# Revit family: A61_63_UN_Line Pendant_ETK
name_source: partatom
category: Lighting Fixtures
units: mm (PartAtom-declared; Revit-internal decimal feet)

## family parameters
Always vertical = Yes
Cut with Voids When Loaded = No
Light Source = Yes
OmniClass Number = 23.80.70.11.14.11
OmniClass Title = Downlights
Part Type = Normal
Room Calculation Point = Yes
Round Connector Dimension = Use Diameter
Shared = No
Work Plane-Based = No

## types (56) — shared parameters
Assembly Code = 63.0
Color Filter = 16777215
Dimming Lamp Color Temperature Shift = <None>
ETIM Code = ETIMCODE
Emit Shape Visible in Rendering = No
Emit from Rectangle Length = 41 mm  [stored 0.134514 ft]
GTIN Code = GTINCODE
H1 = 82 mm  [stored 0.269029 ft]
Housing_Material = Select RGB Value for different appearance
IK Value = -
IP Value = IP20
ISBN Code = ISBNCODE
IfcExportAs = IfcLightFixtureType
IfcExportType = USERDEFINED
L2 = 45 mm  [stored 0.147638 ft]
L3 = 2 mm  [stored 0.00656168 ft]
LED Panel = Yes
Lamp = LED
Model = A61
Tilt Angle = 90.00°
Type Comments = Line Pendant
URL = www.etk.nl
Voltage = 230 V
zero-valued in all types: Calc_L2_Symbol

## per-type parameters (varying)
| type | Apparent Load | Calc_L1_Symbol | Emit from Rectangle Width | L1 | L4 | Luminous Flux (lm) | Manufacturer | Photometric Web File | Wattage Comments |
| A61.2 LED 82W 4000K 12000Lm zwart mat RAL9005 DALI voedingsmodule 2805mm LINEpro light pendel (A6-604PL.A280.40.06/DIMM 2-3) | 82 VA | 28 mm | 2801 mm  [stored 9.18963 ft] | 2805 mm  [stored 9.20276 ft] | 2605 mm  [stored 8.54659 ft] | 6618 lm | ETK B.V. | A61.2863.35_LDT.ies | 82 |
| A61.2 LED 82W 4000K 12000Lm wit mat RAL9003 DALI voedingsmodule 2805mm LINEpro light pendel (A6-604PL.A280.40.08/DIMM 2-3) | 82 VA | 28 mm | 2801 mm  [stored 9.18963 ft] | 2805 mm  [stored 9.20276 ft] | 2605 mm  [stored 8.54659 ft] | 6618 lm | ETK B.V. | A61.2863.15_LDT.ies | 82 |
| A61.2 LED 82W 4000K 12000Lm wit mat RAL9003 voedingsmodule 2805mm LINEpro light pendel (A6-604PL.A280.40.08) | 82 VA | 28 mm | 2801 mm  [stored 9.18963 ft] | 2805 mm  [stored 9.20276 ft] | 2605 mm  [stored 8.54659 ft] | 6618 lm | ETK B.V. | A61.2860.15_LDT.ies | 82 |
| A61.2 LED 82W 4000K 12000Lm zwart mat RAL9005 voedingsmodule 2805mm LINEpro light pendel (A6-604PL.A280.40.06) | 82 VA | 28 mm | 2801 mm  [stored 9.18963 ft] | 2805 mm  [stored 9.20276 ft] | 2605 mm  [stored 8.54659 ft] | 6618 lm | ETK B.V. | A61.2860.35_LDT.ies | 82 |
| A61.2 LED 82W 3000K 11510Lm zwart mat RAL9005 voedingsmodule 2805mm LINEpro light pendel (A6-604PL.A280.30.06) | 82 VA | 28 mm | 2801 mm  [stored 9.18963 ft] | 2805 mm  [stored 9.20276 ft] | 2605 mm  [stored 8.54659 ft] | 6346 lm | ETK B.V. | A61.2810.35_LDT.ies | 82 |
| A61.2 LED 82W 3000K 11510Lm wit mat RAL9003 voedingsmodule 2805mm LINEpro light pendel (A6-604PL.A280.30.08) | 82 VA | 28 mm | 2801 mm  [stored 9.18963 ft] | 2805 mm  [stored 9.20276 ft] | 2605 mm  [stored 8.54659 ft] | 6346 lm | ETK B.V. | A61.2810.15_LDT.ies | 82 |
| A61.2 LED 82W 3000K 11510Lm wit mat RAL9003 DALI voedingsmodule 2805mm LINEpro light pendel (A6-604PL.A280.30.08/DIMM 2-3) | 82 VA | 28 mm | 2801 mm  [stored 9.18963 ft] | 2805 mm  [stored 9.20276 ft] | 2605 mm  [stored 8.54659 ft] | 6346 lm | ETK B.V. | A61.2813.15_LDT.ies | 82 |
| A61.2 LED 82W 3000K 11510Lm zwart mat RAL9005 DALI voedingsmodule 2805mm LINEpro light pendel (A6-604PL.A280.30.06/DIMM 2-3) | 82 VA | 28 mm | 2801 mm  [stored 9.18963 ft] | 2805 mm  [stored 9.20276 ft] | 2605 mm  [stored 8.54659 ft] | 6346 lm | ETK B.V. | A61.2813.35_LDT.ies | 82 |
| A61.2 LED 75W 4000K 10800Lm wit mat RAL9003 voedingsmodule 2525mm LINEpro light pendel (A6-604PL.A252.40.08) | 75 VA | 25 mm  [stored 0.082021 ft] | 2521 mm | 2525 mm  [stored 8.28412 ft] | 2325 mm | 5956 lm | ETK B.V. | A61.2760.15_LDT.ies | 75 |
| A61.2 LED 75W 4000K 10800Lm wit mat RAL9003 DALI voedingsmodule 2525mm LINEpro light pendel (A6-604PL.A252.40.08/DIMM 2-3) | 75 VA | 25 mm  [stored 0.082021 ft] | 2521 mm | 2525 mm  [stored 8.28412 ft] | 2325 mm | 5956 lm | ETK B.V. | A61.2763.15_LDT.ies | 75 |
| A61.2 LED 75W 4000K 10800Lm zwart mat RAL9005 voedingsmodule 2525mm LINEpro light pendel (A6-604PL.A252.40.06) | 75 VA | 25 mm  [stored 0.082021 ft] | 2521 mm | 2525 mm  [stored 8.28412 ft] | 2325 mm | 5956 lm | ETK B.V. | A61.2760.35_LDT.ies | 75 |
| A61.2 LED 75W 4000K 10800Lm zwart mat RAL9005 DALI voedingsmodule 2525mm LINEpro light pendel (A6-604PL.A252.40.06/DIMM 2-3) | 75 VA | 25 mm  [stored 0.082021 ft] | 2521 mm | 2525 mm  [stored 8.28412 ft] | 2325 mm | 5956 lm | ETK B.V. | A61.2763.35_LDT.ies | 75 |
| A61.2 LED 75W 3000K 10360Lm zwart mat RAL9005 voedingsmodule 2525mm LINEpro light pendel (A6-604PL.A252.30.06) | 75 VA | 25 mm  [stored 0.082021 ft] | 2521 mm | 2525 mm  [stored 8.28412 ft] | 2325 mm | 5712 lm | ETK B.V. | A61.2710.35_LDT.ies | 75 |
| A61.2 LED 75W 3000K 10360Lm wit mat RAL9003 DALI voedingsmodule 2525mm LINEpro light pendel (A6-604PL.A252.30.08/DIMM 2-3) | 75 VA | 25 mm  [stored 0.082021 ft] | 2521 mm | 2525 mm  [stored 8.28412 ft] | 2325 mm | 5712 lm | ETK B.V. | A61.2713.15_LDT.ies | 75 |
| A61.2 LED 75W 3000K 10360Lm zwart mat RAL9005 DALI voedingsmodule 2525mm LINEpro light pendel (A6-604PL.A252.30.06/DIMM 2-3) | 75 VA | 25 mm  [stored 0.082021 ft] | 2521 mm | 2525 mm  [stored 8.28412 ft] | 2325 mm | 5712 lm | ETK B.V. | A61.2713.35_LDT.ies | 75 |
| A61.2 LED 75W 3000K 10360Lm wit mat RAL9003 voedingsmodule 2525mm LINEpro light pendel (A6-604PL.A252.30.08) | 75 VA | 25 mm  [stored 0.082021 ft] | 2521 mm | 2525 mm  [stored 8.28412 ft] | 2325 mm | 5712 lm | ETK B.V. | A61.2710.15_LDT.ies | 75 |
| A61.2 LED 67W 4000K 9600Lm zwart mat RAL9005 voedingsmodule 2245mm LINEpro light pendel (A6-604PL.A224.40.06) | 67 VA | 22 mm | 2241 mm  [stored 7.35236 ft] | 2245 mm  [stored 7.36549 ft] | 2045 mm  [stored 6.70932 ft] | 5294 lm | ETK B.V. | A61.2660.35_LDT.ies | 67 |
| A61.2 LED 67W 4000K 9600Lm wit mat RAL9003 DALI voedingsmodule 2245mm LINEpro light pendel (A6-604PL.A224.40.08/DIMM 2-3) | 67 VA | 22 mm | 2241 mm  [stored 7.35236 ft] | 2245 mm  [stored 7.36549 ft] | 2045 mm  [stored 6.70932 ft] | 5294 lm | ETK B.V. | A61.2663.15_LDT.ies | 67 |
| A61.2 LED 67W 4000K 9600Lm wit mat RAL9003 voedingsmodule 2245mm LINEpro light pendel (A6-604PL.A224.40.08) | 67 VA | 22 mm | 2241 mm  [stored 7.35236 ft] | 2245 mm  [stored 7.36549 ft] | 2045 mm  [stored 6.70932 ft] | 5294 lm | ETK B.V. | A61.2660.15_LDT.ies | 67 |
| A61.2 LED 67W 4000K 9600Lm zwart mat RAL9005 DALI voedingsmodule 2245mm LINEpro light pendel (A6-604PL.A224.40.06/DIMM 2-3) | 67 VA | 22 mm | 2241 mm  [stored 7.35236 ft] | 2245 mm  [stored 7.36549 ft] | 2045 mm  [stored 6.70932 ft] | 5294 lm | ETK B.V. | A61.2663.35_LDT.ies | 67 |
| A61.2 LED 67W 3000K 9205Lm zwart mat RAL9005 voedingsmodule 2245mm LINEpro light pendel (A6-604PL.A224.30.06) | 67 VA | 22 mm | 2241 mm  [stored 7.35236 ft] | 2245 mm  [stored 7.36549 ft] | 2045 mm  [stored 6.70932 ft] | 5078 lm | ETK B.V. | A61.2610.35_LDT.ies | 67 |
| A61.2 LED 67W 3000K 9205Lm wit mat RAL9003 DALI voedingsmodule 2245mm LINEpro light pendel (A6-604PL.A224.30.08/DIMM 2-3) | 67 VA | 22 mm | 2241 mm  [stored 7.35236 ft] | 2245 mm  [stored 7.36549 ft] | 2045 mm  [stored 6.70932 ft] | 5078 lm | ETK B.V. | A61.2613.15_LDT.ies | 67 |
| A61.2 LED 67W 3000K 9205Lm wit mat RAL9003 voedingsmodule 2245mm LINEpro light pendel (A6-604PL.A224.30.08) | 67 VA | 22 mm | 2241 mm  [stored 7.35236 ft] | 2245 mm  [stored 7.36549 ft] | 2045 mm  [stored 6.70932 ft] | 5078 lm | ETK B.V. | A61.2610.15_LDT.ies | 67 |
| A61.2 LED 67W 3000K 9205Lm zwart mat RAL9005 DALI voedingsmodule 2245mm LINEpro light pendel (A6-604PL.A224.30.06/DIMM 2-3) | 67 VA | 22 mm | 2241 mm  [stored 7.35236 ft] | 2245 mm  [stored 7.36549 ft] | 2045 mm  [stored 6.70932 ft] | 5078 lm | ETK B.V. | A61.2613.35_LDT.ies | 67 |
| A61.2 LED 60W 4000K 8400Lm wit mat RAL9003 DALI voedingsmodule 1965mm LINEpro light pendel (A6-604PL.A196.40.08/DIMM 2-3) | 60 VA | 20 mm  [stored 0.0656168 ft] | 1961 mm  [stored 6.43373 ft] | 1965 mm  [stored 6.44685 ft] | 1765 mm  [stored 5.79068 ft] | 4633 lm | ETK B.V. | A61.2563.15_LDT.ies | 60 |
| A61.2 LED 60W 4000K 8400Lm zwart mat RAL9005 voedingsmodule 1965mm LINEpro light pendel (A6-604PL.A196.40.06) | 60 VA | 20 mm  [stored 0.0656168 ft] | 1961 mm  [stored 6.43373 ft] | 1965 mm  [stored 6.44685 ft] | 1765 mm  [stored 5.79068 ft] | 4633 lm | ETK B.V. | A61.2560.35_LDT.ies | 60 |
| A61.2 LED 60W 4000K 8400Lm wit mat RAL9003 voedingsmodule 1965mm LINEpro light pendel (A6-604PL.A196.40.08) | 60 VA | 20 mm  [stored 0.0656168 ft] | 1961 mm  [stored 6.43373 ft] | 1965 mm  [stored 6.44685 ft] | 1765 mm  [stored 5.79068 ft] | 4633 lm | ETK B.V. | A61.2560.15_LDT.ies | 60 |
| A61.2 LED 60W 4000K 8400Lm zwart mat RAL9005 DALI voedingsmodule 1965mm LINEpro light pendel (A6-604PL.A196.40.06/DIMM 2-3) | 60 VA | 20 mm  [stored 0.0656168 ft] | 1961 mm  [stored 6.43373 ft] | 1965 mm  [stored 6.44685 ft] | 1765 mm  [stored 5.79068 ft] | 4633 lm | ETK B.V. | A61.2563.35_LDT.ies | 60 |
| A61.2 LED 60W 3000K 8055Lm wit mat RAL9003 voedingsmodule 1965mm LINEpro light pendel (A6-604PL.A196.30.08) | 60 VA | 20 mm  [stored 0.0656168 ft] | 1961 mm  [stored 6.43373 ft] | 1965 mm  [stored 6.44685 ft] | 1765 mm  [stored 5.79068 ft] | 4442 lm | ETK B.V. | A61.2510.15_LDT.ies | 60 |
| A61.2 LED 60W 3000K 8055Lm zwart mat RAL9005 voedingsmodule 1965mm LINEpro light pendel (A6-604PL.A196.30.06) | 60 VA | 20 mm  [stored 0.0656168 ft] | 1961 mm  [stored 6.43373 ft] | 1965 mm  [stored 6.44685 ft] | 1765 mm  [stored 5.79068 ft] | 4442 lm | ETK B.V. | A61.2510.35_LDT.ies | 60 |
| A61.2 LED 60W 3000K 8055Lm zwart mat RAL9005 DALI voedingsmodule 1965mm LINEpro light pendel (A6-604PL.A196.30.06/DIMM 2-3) | 60 VA | 20 mm  [stored 0.0656168 ft] | 1961 mm  [stored 6.43373 ft] | 1965 mm  [stored 6.44685 ft] | 1765 mm  [stored 5.79068 ft] | 4442 lm | ETK B.V. | A61.2513.35_LDT.ies | 60 |
| A61.2 LED 60W 3000K 8055Lm wit mat RAL9003 DALI voedingsmodule 1965mm LINEpro light pendel (A6-604PL.A196.30.08/DIMM 2-3) | 60 VA | 20 mm  [stored 0.0656168 ft] | 1961 mm  [stored 6.43373 ft] | 1965 mm  [stored 6.44685 ft] | 1765 mm  [stored 5.79068 ft] | 4442 lm | ETK B.V. | A61.2513.15_LDT.ies | 60 |
| A61.2 LED 51W 4000K 7200Lm wit mat RAL9003 voedingsmodule 1685mm LINEpro light pendel (A6-604PL.A168.40.08) | 51 VA | 17 mm | 1681 mm  [stored 5.51509 ft] | 1685 mm  [stored 5.52822 ft] | 1485 mm  [stored 4.87205 ft] | 3971 lm | ETK B.V. | A61.2460.15_LDT.ies | 51 |
| A61.2 LED 51W 4000K 7200Lm wit mat RAL9003 DALI voedingsmodule 1685mm LINEpro light pendel (A6-604PL.A168.40.08/DIMM 2-3) | 51 VA | 17 mm | 1681 mm  [stored 5.51509 ft] | 1685 mm  [stored 5.52822 ft] | 1485 mm  [stored 4.87205 ft] | 3971 lm | ETK B.V. | A61.2463.15_LDT.ies | 51 |
| A61.2 LED 51W 4000K 7200Lm zwart mat RAL9005 DALI voedingsmodule 1685mm LINEpro light pendel (A6-604PL.A168.40.06/DIMM 2-3) | 51 VA | 17 mm | 1681 mm  [stored 5.51509 ft] | 1685 mm  [stored 5.52822 ft] | 1485 mm  [stored 4.87205 ft] | 3971 lm | ETK B.V. | A61.2463.35_LDT.ies | 51 |
| A61.2 LED 51W 4000K 7200Lm zwart mat RAL9005 voedingsmodule 1685mm LINEpro light pendel (A6-604PL.A168.40.06) | 51 VA | 17 mm | 1681 mm  [stored 5.51509 ft] | 1685 mm  [stored 5.52822 ft] | 1485 mm  [stored 4.87205 ft] | 3971 lm | ETK B.V. | A61.2460.35_LDT.ies | 51 |
| A61.2 LED 51W 3000K 6905Lm wit mat RAL9003 DALI voedingsmodule 1685mm LINEpro light pendel (A6-604PL.A168.30.08/DIMM 2-3) | 51 VA | 17 mm | 1681 mm  [stored 5.51509 ft] | 1685 mm  [stored 5.52822 ft] | 1485 mm  [stored 4.87205 ft] | 3808 lm | ETK B.V. | A61.2413.15_LDT.ies | 51 |
| A61.2 LED 51W 3000K 6905Lm zwart mat RAL9005 voedingsmodule 1685mm LINEpro light pendel (A6-604PL.A168.30.06) | 51 VA | 17 mm | 1681 mm  [stored 5.51509 ft] | 1685 mm  [stored 5.52822 ft] | 1485 mm  [stored 4.87205 ft] | 3808 lm | ETK B.V. | A61.2410.35_LDT.ies | 51 |
| A61.2 LED 51W 3000K 6905Lm wit mat RAL9003 voedingsmodule 1685mm LINEpro light pendel (A6-604PL.A168.30.08) | 51 VA | 17 mm | 1681 mm  [stored 5.51509 ft] | 1685 mm  [stored 5.52822 ft] | 1485 mm  [stored 4.87205 ft] | 3808 lm | ETK B.V. | A61.2410.15_LDT.ies | 51 |
| A61.2 LED 51W 3000K 6905Lm zwart mat RAL9005 DALI voedingsmodule 1685mm LINEpro light pendel (A6-604PL.A168.30.06/DIMM 2-3) | 51 VA | 17 mm | 1681 mm  [stored 5.51509 ft] | 1685 mm  [stored 5.52822 ft] | 1485 mm  [stored 4.87205 ft] | 3808 lm | ETK B.V. | A61.2413.35_LDT.ies | 51 |
| A61.2 LED 44W 3000K 5755Lm zwart mat RAL9005 voedingsmodule 1405mm LINEpro light pendel (A6-604PL.A140.30.06) | 44 VA | 14 mm  [stored 0.0459318 ft] | 1401 mm | 1405 mm  [stored 4.60958 ft] | 1205 mm  [stored 3.95341 ft] | 3173 lm | ETK B.V. | A61.2310.35_LDT.ies | 44 |
| A61.2 LED 44W 3000K 5755Lm wit mat RAL9003 DALI voedingsmodule 1405mm LINEpro light pendel (A6-604PL.A140.30.08/DIMM 2-3) | 44 VA | 14 mm  [stored 0.0459318 ft] | 1401 mm | 1405 mm  [stored 4.60958 ft] | 1205 mm  [stored 3.95341 ft] | 3173 lm | ETK B.V. | A61.2313.15_LDT.ies | 44 |
| A61.2 LED 44W 3000K 5755Lm zwart mat RAL9005 DALI voedingsmodule 1405mm LINEpro light pendel (A6-604PL.A140.30.06/DIMM 2-3) | 44 VA | 14 mm  [stored 0.0459318 ft] | 1401 mm | 1405 mm  [stored 4.60958 ft] | 1205 mm  [stored 3.95341 ft] | 3173 lm | ETK B.V. | A61.2313.35_LDT.ies | 44 |
| A61.2 LED 44W 3000K 5755Lm wit mat RAL9003 voedingsmodule 1405mm LINEpro light pendel (A6-604PL.A140.30.08) | 44 VA | 14 mm  [stored 0.0459318 ft] | 1401 mm | 1405 mm  [stored 4.60958 ft] | 1205 mm  [stored 3.95341 ft] | 3173 lm | ETK B.V. | A61.2310.15_LDT.ies | 44 |
| A61.2 LED 44W 4000K 6000Lm zwart mat RAL9005 voedingsmodule 1405mm LINEpro light pendel (A6-604PL.A140.40.06) | 44 VA | 14 mm  [stored 0.0459318 ft] | 1401 mm | 1405 mm  [stored 4.60958 ft] | 1205 mm  [stored 3.95341 ft] | 3309 lm | ETK B.V. | A61.2360.35_LDT.ies | 44 |
| A61.2 LED 44W 4000K 6000Lm wit mat RAL9003 DALI voedingsmodule 1405mm LINEpro light pendel (A6-604PL.A140.40.08/DIMM 2-3) | 44 VA | 14 mm  [stored 0.0459318 ft] | 1401 mm | 1405 mm  [stored 4.60958 ft] | 1205 mm  [stored 3.95341 ft] | 3309 lm | ETK B.V. | A61.2363.15_LDT.ies | 44 |
| A61.2 LED 44W 4000K 6000Lm wit mat RAL9003 voedingsmodule 1405mm LINEpro light pendel (A6-604PL.A140.40.08) | 44 VA | 14 mm  [stored 0.0459318 ft] | 1401 mm | 1405 mm  [stored 4.60958 ft] | 1205 mm  [stored 3.95341 ft] | 3309 lm | ETK B.V. | A61.2360.15_LDT.ies | 44 |
| A61.2 LED 44W 4000K 6000Lm zwart mat RAL9005 DALI voedingsmodule 1405mm LINEpro light pendel (A6-604PL.A140.40.06/DIMM 2-3) | 44 VA | 14 mm  [stored 0.0459318 ft] | 1401 mm | 1405 mm  [stored 4.60958 ft] | 1205 mm  [stored 3.95341 ft] | 3309 lm | ETK B.V. | A61.2363.35_LDT.ies | 44 |
| A61.2 LED 35W 4000K 4800Lm zwart mat RAL9005 voedingsmodule 1125mm LINEpro light pendel (A6-604PL.A112.40.06) | 35 VA | 11 mm | 1121 mm  [stored 3.67782 ft] | 1125 mm | 925 mm  [stored 3.03478 ft] | 2647 lm | ETK | A61.2260.35_LDT.ies | 35 |
| A61.2 LED 35W 4000K 4800Lm wit mat RAL9003 voedingsmodule 1125mm LINEpro light pendel (A6-604PL.A112.40.08) | 35 VA | 11 mm | 1121 mm  [stored 3.67782 ft] | 1125 mm | 925 mm  [stored 3.03478 ft] | 2647 lm | ETK | A61.2260.15_LDT.ies | 35 |
| A61.2 LED 35W 4000K 4800Lm zwart mat RAL9005 DALI voedingsmodule 1125mm LINEpro light pendel (A6-604PL.A112.40.06/DIMM 2-3) | 35 VA | 11 mm | 1121 mm  [stored 3.67782 ft] | 1125 mm | 925 mm  [stored 3.03478 ft] | 2647 lm | ETK | A61.2263.35_LDT.ies | 35 |
| A61.2 LED 35W 4000K 4800Lm wit mat RAL9003 DALI voedingsmodule 1125mm LINEpro light pendel (A6-604PL.A112.40.08/DIMM 2-3) | 35 VA | 11 mm | 1121 mm  [stored 3.67782 ft] | 1125 mm | 925 mm  [stored 3.03478 ft] | 2647 lm | ETK | A61.2263.15_LDT.ies | 35 |
| A61.2 LED 35W 3000K 4600Lm wit mat RAL9003 voedingsmodule 1125mm LINEpro light pendel (A6-604PL.A112.30.08) | 35 VA | 11 mm | 1121 mm  [stored 3.67782 ft] | 1125 mm | 925 mm  [stored 3.03478 ft] | 2539 lm | ETK | A61.2210.15_LDT.ies | 35 |
| A61.2 LED 35W 3000K 4600Lm wit mat RAL9003 DALI voedingsmodule 1125mm LINEpro light pendel (A6-604PL.A112.30.08/DIMM 2-3) | 35 VA | 11 mm | 1121 mm  [stored 3.67782 ft] | 1125 mm | 925 mm  [stored 3.03478 ft] | 2539 lm | ETK | A61.2213.15_LDT.ies | 35 |
| A61.2 LED 35W 3000K 4600Lm zwart mat RAL9005 DALI voedingsmodule 1125mm LINEpro light pendel (A6-604PL.A112.30.06/DIMM 2-3) | 35 VA | 11 mm | 1121 mm  [stored 3.67782 ft] | 1125 mm | 925 mm  [stored 3.03478 ft] | 2539 lm | ETK | A61.2213.35_LDT.ies | 35 |
| A61.2 LED 35W 3000K 4600Lm zwart mat RAL9005 voedingsmodule 1125mm LINEpro light pendel (A6-604PL.A112.30.06) | 35 VA | 11 mm | 1121 mm  [stored 3.67782 ft] | 1125 mm | 925 mm  [stored 3.03478 ft] | 2539 lm | ETK | A61.2210.35_LDT.ies | 35 |

note: [stored X ft] marks values corroborated as IEEE doubles in the binary element streams (Revit-internal decimal feet)

## geometry (parser evidence)
native form markers: Sweep x3
no freeform markers — native parametric forms only
